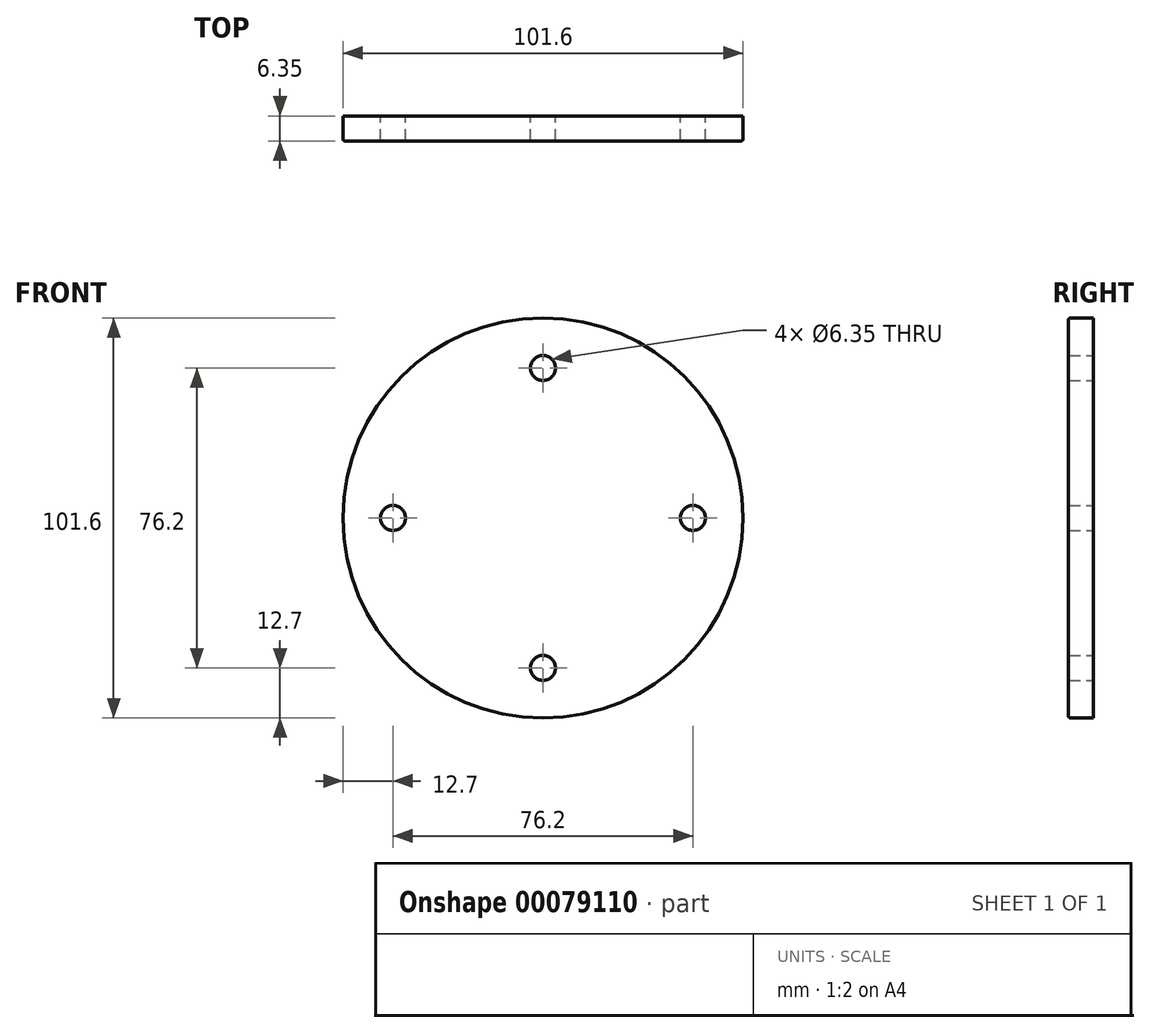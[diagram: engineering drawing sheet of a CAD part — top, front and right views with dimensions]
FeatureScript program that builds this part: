
annotation { "Feature Type Name" : "Feature", "Feature Type Description" : "" }
export const myFeature = defineFeature(function(context is Context, id is Id, definition is map)
    precondition{}
    {
        {
            var Q0;
            Q0=qCreatedBy(makeId("Front.planeOp"),FACE);
            var sketch = newSketch(context, id + "F0", { "sketchPlane" : qUnion([Q0])});
            skCircle(sketch, "E0", {"center": v(0, 0) * mm, "radius": 50.8 * mm});
            skCircle(sketch, "E1", {"center": v(-38.1, 0) * mm, "radius": 3.18 * mm});
            skCircle(sketch, "E2", {"center": v(0, 38.1) * mm, "radius": 3.18 * mm});
            skCircle(sketch, "E3", {"center": v(38.1, 0) * mm, "radius": 3.18 * mm});
            skCircle(sketch, "E4", {"center": v(0, -38.1) * mm, "radius": 3.18 * mm});
            skSolve(sketch);
        }
        {
            var Q0;
            Q0 = qSketchRegion(id + "F0", true);
            extrude(context, id + "F1", {"entities" : qUnion([Q0]), "depth" : 6.35 * mm});
        }
        {
            var Q0;
            Q0=makeQuery(id+"F1.opExtrude","CAP_EDGE",EDGE,{"disambiguationData":[OSD([sQuery(id+"F0.wireOp",EDGE,"E0")])],"isStart":false});
            fillet(context, id + "F2", {"entities" : qUnion([Q0]), "radius" : 0.44 * mm, "tangentPropagation" : true, "allowEdgeOverflow" : false});
        }
    });
